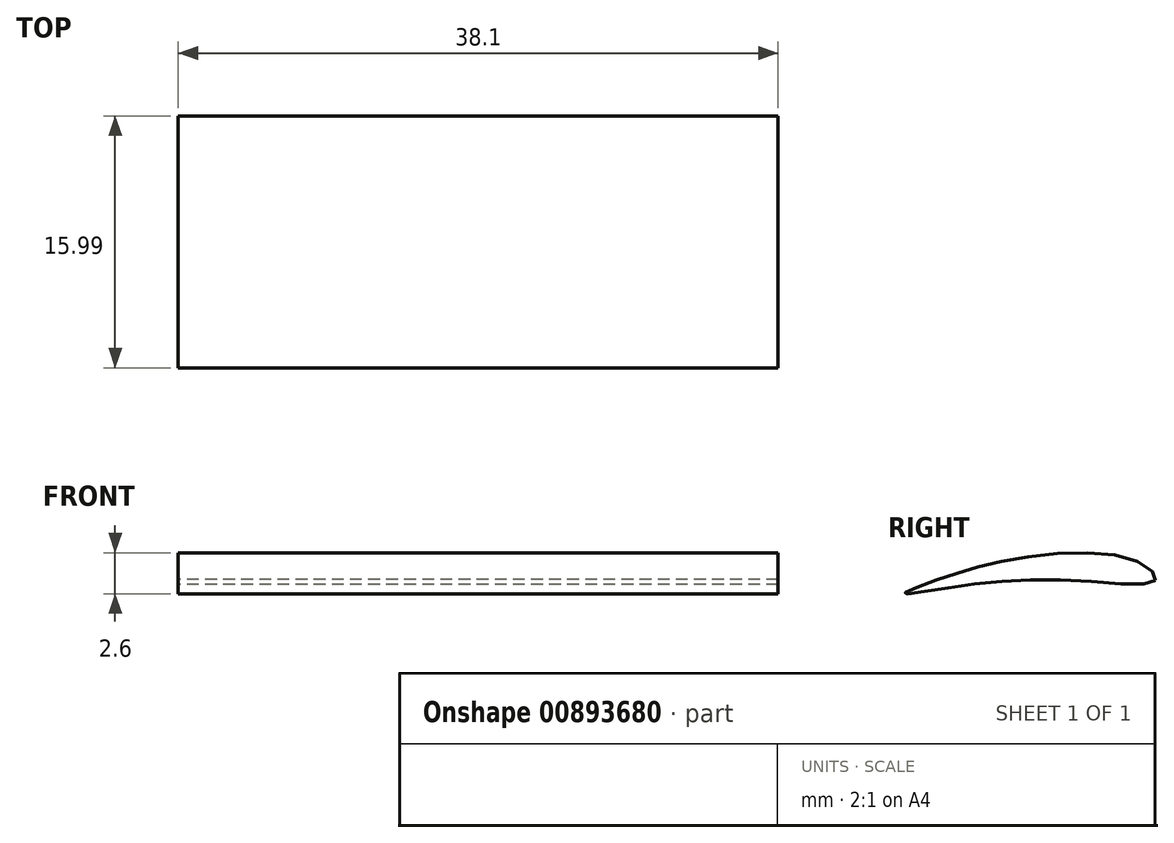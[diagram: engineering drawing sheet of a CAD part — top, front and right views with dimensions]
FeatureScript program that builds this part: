
annotation { "Feature Type Name" : "Feature", "Feature Type Description" : "" }
export const myFeature = defineFeature(function(context is Context, id is Id, definition is map)
    precondition{}
    {
        {
            var Q0;
            Q0=qCreatedBy(makeId("Right.planeOp"),FACE);
            var sketch = newSketch(context, id + "F0", { "sketchPlane" : qUnion([Q0])});
            skFitSpline(sketch, "E0", {"points": [v(7.86, -0.4) * mm, v(6.65, 0.83) * mm, v(-0.92, 0.98) * mm, v(-6.07, -0.4) * mm, v(-8.09, -1.24) * mm, v(-5.36, -0.89) * mm, v(2.61, -0.4) * mm, v(7.86, -0.4) * mm]});
            skSolve(sketch);
        }
        {
            var Q0;
            Q0=makeQuery(id+"F0.imprint","IMPRINT",FACE,{"disambiguationData":[TD([[makeQuery(id+"F0.imprint","IMPRINT",EDGE,{"derivedFrom":sQuery(id+"F0.wireOp",EDGE,"E0")}),1.0]])]});
            extrude(context, id + "F1", {"entities" : qUnion([Q0]), "depth" : 38.1 * mm, "offsetDistance" : 25.4 * mm});
        }
    });
